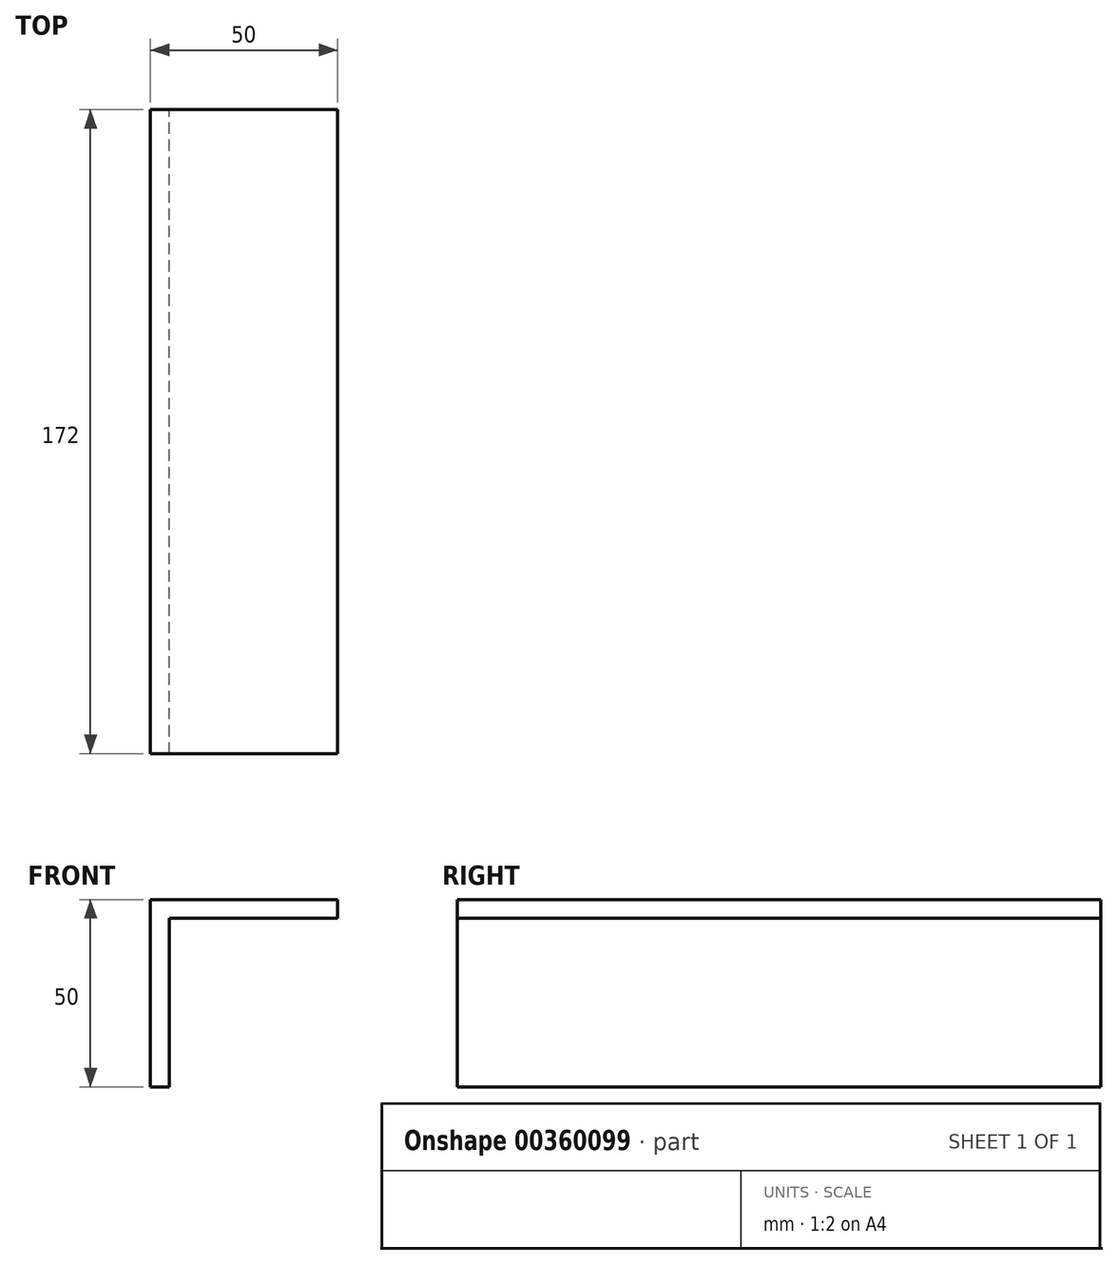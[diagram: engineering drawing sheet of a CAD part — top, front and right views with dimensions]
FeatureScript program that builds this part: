
annotation { "Feature Type Name" : "Feature", "Feature Type Description" : "" }
export const myFeature = defineFeature(function(context is Context, id is Id, definition is map)
    precondition{}
    {
        {
            var Q0;
            Q0=qCreatedBy(makeId("Front.planeOp"),FACE);
            var sketch = newSketch(context, id + "F0", { "sketchPlane" : qUnion([Q0])});
            skLineSegment(sketch, "E0", {"start": v(0, 0) * mm, "end": v(-50, 0) * mm});
            skLineSegment(sketch, "E1", {"start": v(-50, 0) * mm, "end": v(-50, -50) * mm});
            skLineSegment(sketch, "E2", {"start": v(-50, -50) * mm, "end": v(-45, -50) * mm});
            skLineSegment(sketch, "E3", {"start": v(-45, -50) * mm, "end": v(-45, -5) * mm});
            skLineSegment(sketch, "E4", {"start": v(-45, -5) * mm, "end": v(0, -5) * mm});
            skLineSegment(sketch, "E5", {"start": v(0, -5) * mm, "end": v(0, 0) * mm});
            skSolve(sketch);
        }
        {
            var Q0;
            Q0 = qSketchRegion(id + "F0", true);
            extrude(context, id + "F1", {"entities" : qUnion([Q0]), "depth" : 172 * mm});
        }
    });
